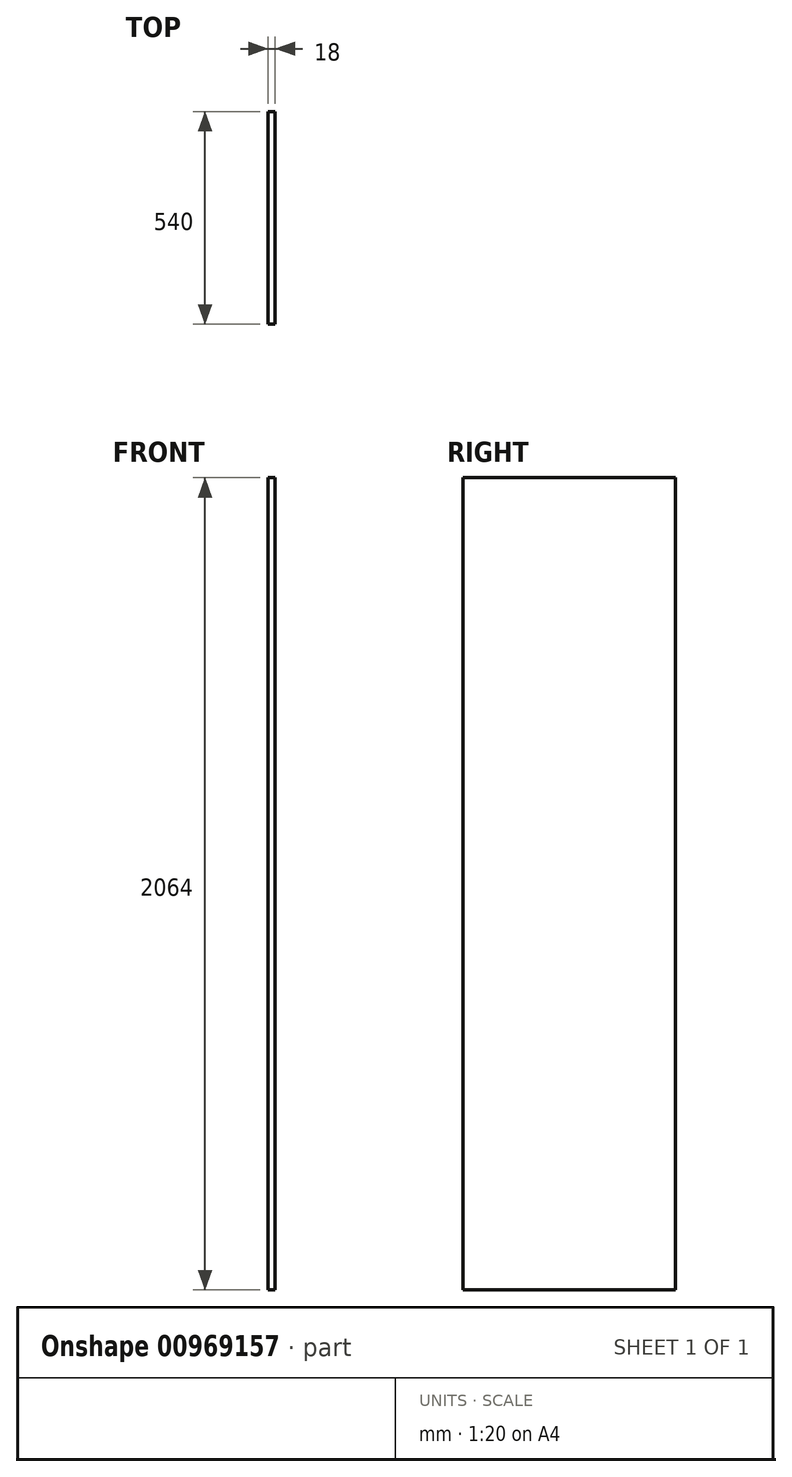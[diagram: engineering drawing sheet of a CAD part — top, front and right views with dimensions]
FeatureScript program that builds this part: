
annotation { "Feature Type Name" : "Feature", "Feature Type Description" : "" }
export const myFeature = defineFeature(function(context is Context, id is Id, definition is map)
    precondition{}
    {
        {
            var Q0;
            Q0=qCreatedBy(makeId("Right.planeOp"),FACE);
            var sketch = newSketch(context, id + "F0", { "sketchPlane" : qUnion([Q0])});
            skLineSegment(sketch, "E0.bottom", {"start": v(0, 0) * mm, "end": v(540, 0) * mm});
            skLineSegment(sketch, "E0.top", {"start": v(0, 2064) * mm, "end": v(540, 2064) * mm});
            skLineSegment(sketch, "E0.left", {"start": v(0, 0) * mm, "end": v(0, 2064) * mm});
            skLineSegment(sketch, "E0.right", {"start": v(540, 0) * mm, "end": v(540, 2064) * mm});
            skSolve(sketch);
        }
        {
            var Q0;
            Q0 = qSketchRegion(id + "F0", true);
            extrude(context, id + "F1", {"entities" : qUnion([Q0]), "depth" : 18 * mm, "offsetDistance" : 25 * mm});
        }
    });
